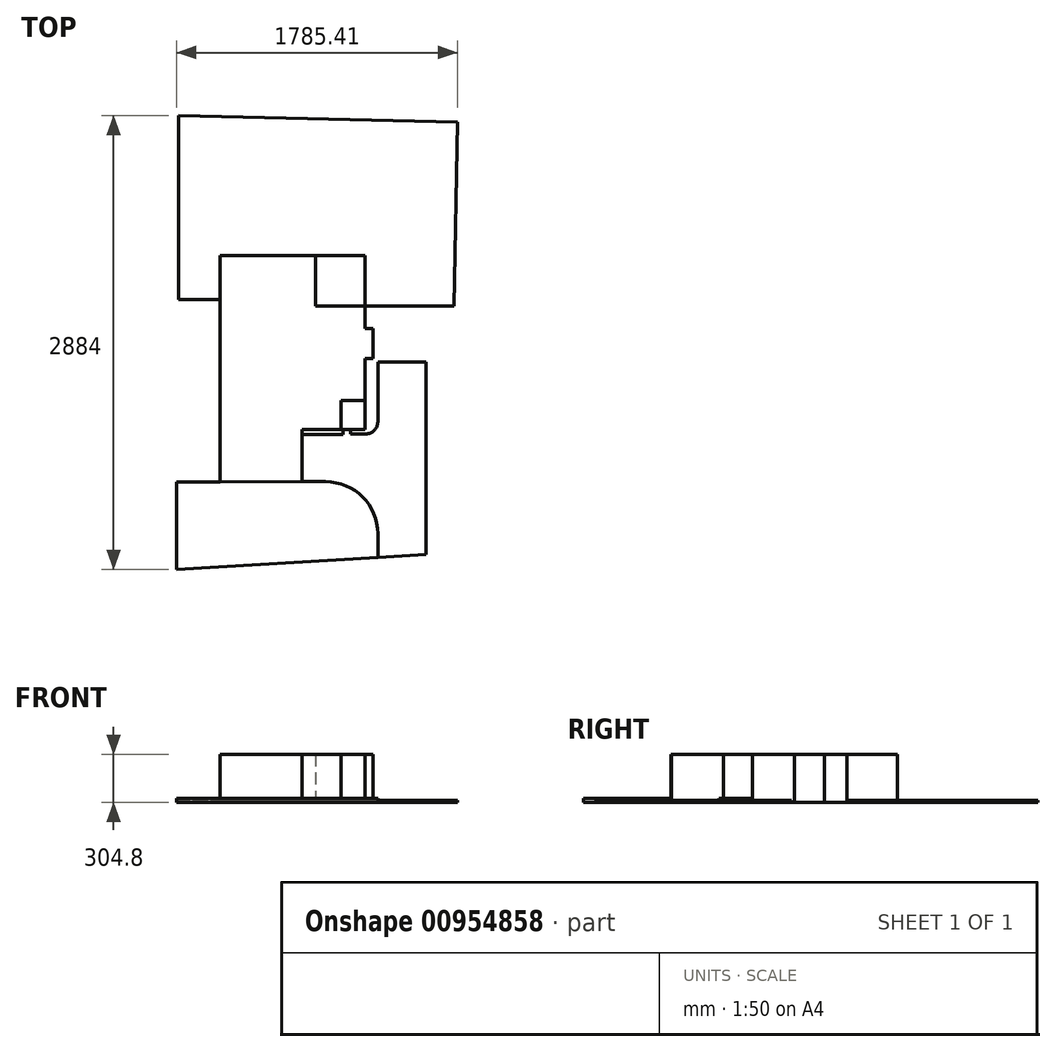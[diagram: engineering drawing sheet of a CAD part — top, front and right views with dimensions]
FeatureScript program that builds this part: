
annotation { "Feature Type Name" : "Feature", "Feature Type Description" : "" }
export const myFeature = defineFeature(function(context is Context, id is Id, definition is map)
    precondition{}
    {
        {
            var Q0;
            Q0=qCreatedBy(makeId("Top.planeOp"),FACE);
            var sketch = newSketch(context, id + "F0", { "sketchPlane" : qUnion([Q0])});
            skLineSegment(sketch, "E0", {"start": v(0, 0) * mm, "end": v(0, 3049.02) * mm});
            skLineSegment(sketch, "E1", {"start": v(0, 3049.02) * mm, "end": v(1795.03, 3006.77) * mm});
            skLineSegment(sketch, "E2", {"start": v(0, 0) * mm, "end": v(1746.85, 106.03) * mm});
            skLineSegment(sketch, "E3", {"start": v(1746.85, 106.03) * mm, "end": v(1795.03, 3006.77) * mm});
            skLineSegment(sketch, "E4", {"start": v(0, 0) * mm, "end": v(0, 556.26) * mm});
            skLineSegment(sketch, "E5", {"start": v(0, 556.26) * mm, "end": v(276.86, 556.26) * mm});
            skLineSegment(sketch, "E6", {"start": v(276.86, 556.26) * mm, "end": v(276.86, 1993.9) * mm});
            skLineSegment(sketch, "E7", {"start": v(276.86, 1993.9) * mm, "end": v(881.38, 1993.9) * mm});
            skLineSegment(sketch, "E8", {"start": v(881.38, 1993.9) * mm, "end": v(881.38, 1673.86) * mm});
            skLineSegment(sketch, "E9", {"start": v(881.38, 1673.86) * mm, "end": v(1196.34, 1673.86) * mm});
            skLineSegment(sketch, "E10", {"start": v(1196.34, 1673.86) * mm, "end": v(1196.34, 1529.08) * mm});
            skLineSegment(sketch, "E11", {"start": v(1196.34, 1529.08) * mm, "end": v(1247.14, 1529.08) * mm});
            skLineSegment(sketch, "E12", {"start": v(1247.14, 1529.08) * mm, "end": v(1247.14, 1338.58) * mm});
            skLineSegment(sketch, "E13", {"start": v(1247.14, 1338.58) * mm, "end": v(1196.34, 1338.58) * mm});
            skLineSegment(sketch, "E14", {"start": v(1196.34, 1338.58) * mm, "end": v(1196.34, 1071.88) * mm});
            skLineSegment(sketch, "E15", {"start": v(1196.34, 1071.88) * mm, "end": v(1043.94, 1071.88) * mm});
            skLineSegment(sketch, "E16", {"start": v(1043.94, 1071.88) * mm, "end": v(1043.94, 887.73) * mm});
            skLineSegment(sketch, "E17", {"start": v(1043.94, 887.73) * mm, "end": v(797.56, 887.73) * mm});
            skLineSegment(sketch, "E18", {"start": v(797.56, 887.73) * mm, "end": v(797.56, 557.53) * mm});
            skLineSegment(sketch, "E19", {"start": v(797.56, 557.53) * mm, "end": v(276.86, 556.26) * mm});
            skLineSegment(sketch, "E20", {"start": v(1043.94, 887.73) * mm, "end": v(1196.34, 887.73) * mm});
            skLineSegment(sketch, "E21", {"start": v(1196.34, 887.73) * mm, "end": v(1196.34, 1071.88) * mm});
            skLineSegment(sketch, "E22", {"start": v(797.56, 858.87) * mm, "end": v(1057.46, 858.87) * mm});
            skLineSegment(sketch, "E23", {"start": v(1057.46, 858.87) * mm, "end": v(1057.46, 887.73) * mm});
            skLineSegment(sketch, "E24", {"start": v(1105.12, 887.73) * mm, "end": v(1105.12, 861.04) * mm});
            skLineSegment(sketch, "E25", {"start": v(1278.23, 1319.01) * mm, "end": v(1278.23, 937.24) * mm});
            skLineSegment(sketch, "E26", {"start": v(1105.12, 861.04) * mm, "end": v(1202.03, 861.04) * mm});
            skLineSegment(sketch, "E27", {"start": v(1628.52, 98.85) * mm, "end": v(1278.23, 77.59) * mm});
            skLineSegment(sketch, "E28", {"start": v(1278.23, 77.59) * mm, "end": v(1278.23, 227.33) * mm});
            skLineSegment(sketch, "E29", {"start": v(797.56, 557.53) * mm, "end": v(948.03, 557.53) * mm});
            skLineSegment(sketch, "E30", {"start": v(1278.23, 1319.01) * mm, "end": v(1583.03, 1319.01) * mm});
            skLineSegment(sketch, "E31", {"start": v(1583.03, 1319.01) * mm, "end": v(1583.03, 96.09) * mm});
            skPoint(sketch, "E32.visualSharp", {"position": v(1278.23, 557.53) * mm});
            skArc(sketch, "E32.filletArc", {"start": v(1278.23, 227.33) * mm, "mid": v(1181.52, 460.82) * mm, "end": v(948.03, 557.53) * mm});
            skPoint(sketch, "E33.visualSharp", {"position": v(1278.23, 861.04) * mm});
            skArc(sketch, "E33.filletArc", {"start": v(1202.03, 861.04) * mm, "mid": v(1255.91, 883.36) * mm, "end": v(1278.23, 937.24) * mm});
            skLineSegment(sketch, "E34", {"start": v(1763.6, 1673.86) * mm, "end": v(1785.4, 2842.26) * mm});
            skLineSegment(sketch, "E35", {"start": v(1785.4, 2842.26) * mm, "end": v(11.9, 2884) * mm});
            skLineSegment(sketch, "E36", {"start": v(11.9, 2884) * mm, "end": v(11.9, 1715.6) * mm});
            skLineSegment(sketch, "E37", {"start": v(11.9, 1715.6) * mm, "end": v(276.86, 1715.6) * mm});
            skLineSegment(sketch, "E38", {"start": v(881.38, 1993.9) * mm, "end": v(1196.34, 1993.9) * mm});
            skLineSegment(sketch, "E39", {"start": v(1196.34, 1993.9) * mm, "end": v(1196.34, 1673.86) * mm});
            skLineSegment(sketch, "E40", {"start": v(1196.34, 1673.86) * mm, "end": v(1763.6, 1673.86) * mm});
            skSolve(sketch);
        }
        {
            var Q0;
            {var subQ6=sQuery(id+"F0.wireOp",EDGE,"E22");Q0=makeQuery(id+"F0.imprint","IMPRINT",FACE,{"disambiguationData":[TD([[makeQuery(id+"F0.imprint","IMPRINT",EDGE,{"derivedFrom":subQ6}),-1.0]])]});}
            extrude(context, id + "F1", {"entities" : qUnion([Q0]), "depth" : 12.7 * mm, "offsetDistance" : 25.4 * mm});
        }
        {
            var Q0;
            Q0=makeQuery(id+"F0.imprint","IMPRINT",FACE,{"disambiguationData":[TD([[makeQuery(id+"F0.imprint","IMPRINT",EDGE,{"derivedFrom":sQuery(id+"F0.wireOp",EDGE,"E6")}),-1.0]])]});
            extrude(context, id + "F2", {"entities" : qUnion([Q0]), "depth" : 304.8 * mm, "offsetDistance" : 25.4 * mm});
        }
        {
            var Q0;
            {var subQ1=sQuery(id+"F0.wireOp",EDGE,"E7");Q0=makeQuery(id+"F0.imprint","IMPRINT",FACE,{"disambiguationData":[TD([[makeQuery(id+"F0.imprint","IMPRINT",EDGE,{"derivedFrom":subQ1}),1.0]])]});}
            extrude(context, id + "F3", {"entities" : qUnion([Q0]), "depth" : 12.7 * mm, "offsetDistance" : 25.4 * mm});
        }
        {
            var Q0;
            Q0=makeQuery(id+"F0.imprint","IMPRINT",FACE,{"disambiguationData":[TD([[makeQuery(id+"F0.imprint","IMPRINT",EDGE,{"derivedFrom":sQuery(id+"F0.wireOp",EDGE,"E0")}),-1.0]])]});
            var Q1;
            {var subQ0=sQuery(id+"F0.wireOp",EDGE,"E4");Q1=makeQuery(id+"F0.imprint","IMPRINT",FACE,{"disambiguationData":[TD([[makeQuery(id+"F0.imprint","IMPRINT",EDGE,{"derivedFrom":subQ0}),-1.0]])]});}
            var Q2;
            Q2=makeQuery(id+"F0.imprint","IMPRINT",FACE,{"disambiguationData":[TD([[makeQuery(id+"F0.imprint","IMPRINT",EDGE,{"derivedFrom":sQuery(id+"F0.wireOp",EDGE,"E15")}),1.0]])]});
            var Q3;
            {var subQ2=sQuery(id+"F0.wireOp",EDGE,"E17");Q3=makeQuery(id+"F0.imprint","IMPRINT",FACE,{"disambiguationData":[TD([[makeQuery(id+"F0.imprint","IMPRINT",EDGE,{"derivedFrom":subQ2}),1.0]])]});}
            extrude(context, id + "F4", {"entities" : qUnion([Q0, Q1, Q2, Q3]), "depth" : 25.4 * mm, "offsetDistance" : 25.4 * mm});
        }
        {
            var Q0;
            Q0=makeQuery(id+"F0.imprint","IMPRINT",FACE,{"disambiguationData":[TD([[makeQuery(id+"F0.imprint","IMPRINT",EDGE,{"derivedFrom":sQuery(id+"F0.wireOp",EDGE,"E8")}),1.0]])]});
            extrude(context, id + "F5", {"entities" : qUnion([Q0]), "depth" : 304.8 * mm, "offsetDistance" : 25.4 * mm});
        }
    });
